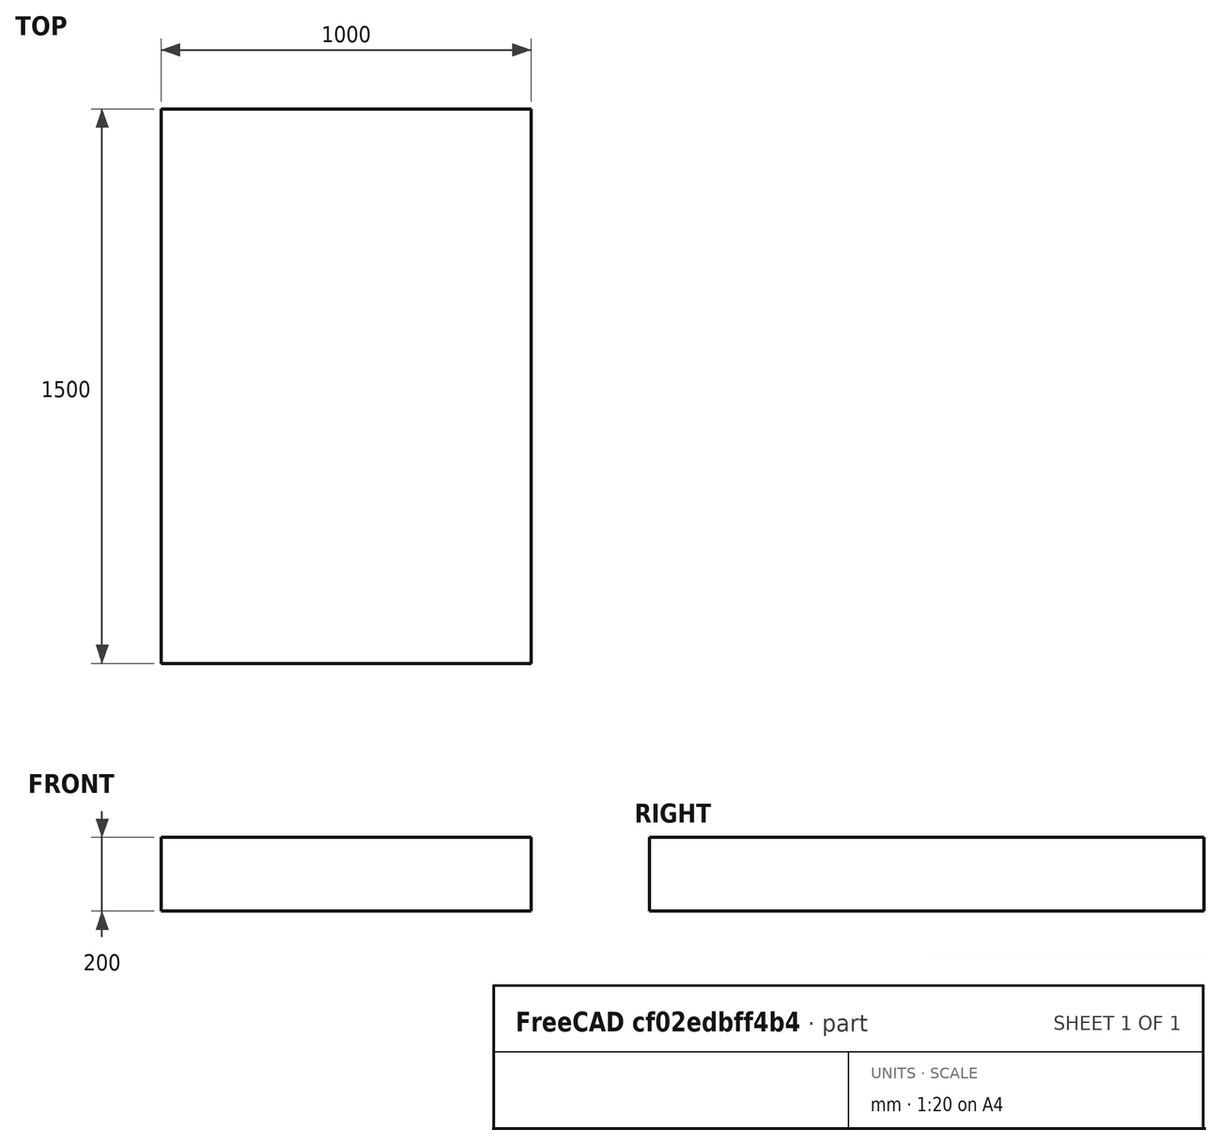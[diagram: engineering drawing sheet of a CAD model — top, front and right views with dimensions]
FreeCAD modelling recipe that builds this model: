
FCSTD DOCUMENT  (FreeCAD 0.19R)
Label: AMR
License: All rights reserved
LicenseURL: http://en.wikipedia.org/wiki/All_rights_reserved
objects: Sketcher::SketchObject×1, PartDesign::Pad×1, PartDesign::Body×1
note: 4 computed .brp shape members not serialized (recipe doc carries the construction recipe); baked Part::Feature solids carry a one-line shape summary decoded from their .brp

FEATURE [Sketcher::SketchObject] Sketch
  FullyConstrained = true
  MapMode = 5
  Support = -> [XY_Plane]
  sketch-geometry (4):
    g0: LineSegment StartX=-500 StartY=750 StartZ=0 EndX=500 EndY=750 EndZ=0
    g1: LineSegment StartX=500 StartY=750 StartZ=0 EndX=500 EndY=-750 EndZ=0
    g2: LineSegment StartX=500 StartY=-750 StartZ=0 EndX=-500 EndY=-750 EndZ=0
    g3: LineSegment StartX=-500 StartY=-750 StartZ=0 EndX=-500 EndY=750 EndZ=0
  constraints (11):
    c: Coincident(g0,g1)
    c: Coincident(g1,g2)
    c: Coincident(g2,g3)
    c: Coincident(g3,g0)
    c: Horizontal(g0)
    c: Horizontal(g2)
    c: Vertical(g1)
    c: Vertical(g3)
    c: Symmetric(g0,g1,g-1)
    c: DistanceX(g0,g0) = 1000
    c: DistanceY(g2,g0) = 1500
FEATURE [PartDesign::Pad] Pad
  Direction = (1,1,1)
  Length = 200
  Length2 = 100
  Profile = -> Sketch
  Type = 0
FEATURE [PartDesign::Body] Body
  Group = -> [Sketch,Pad]
  Origin = -> Origin
  Tip = -> Pad
